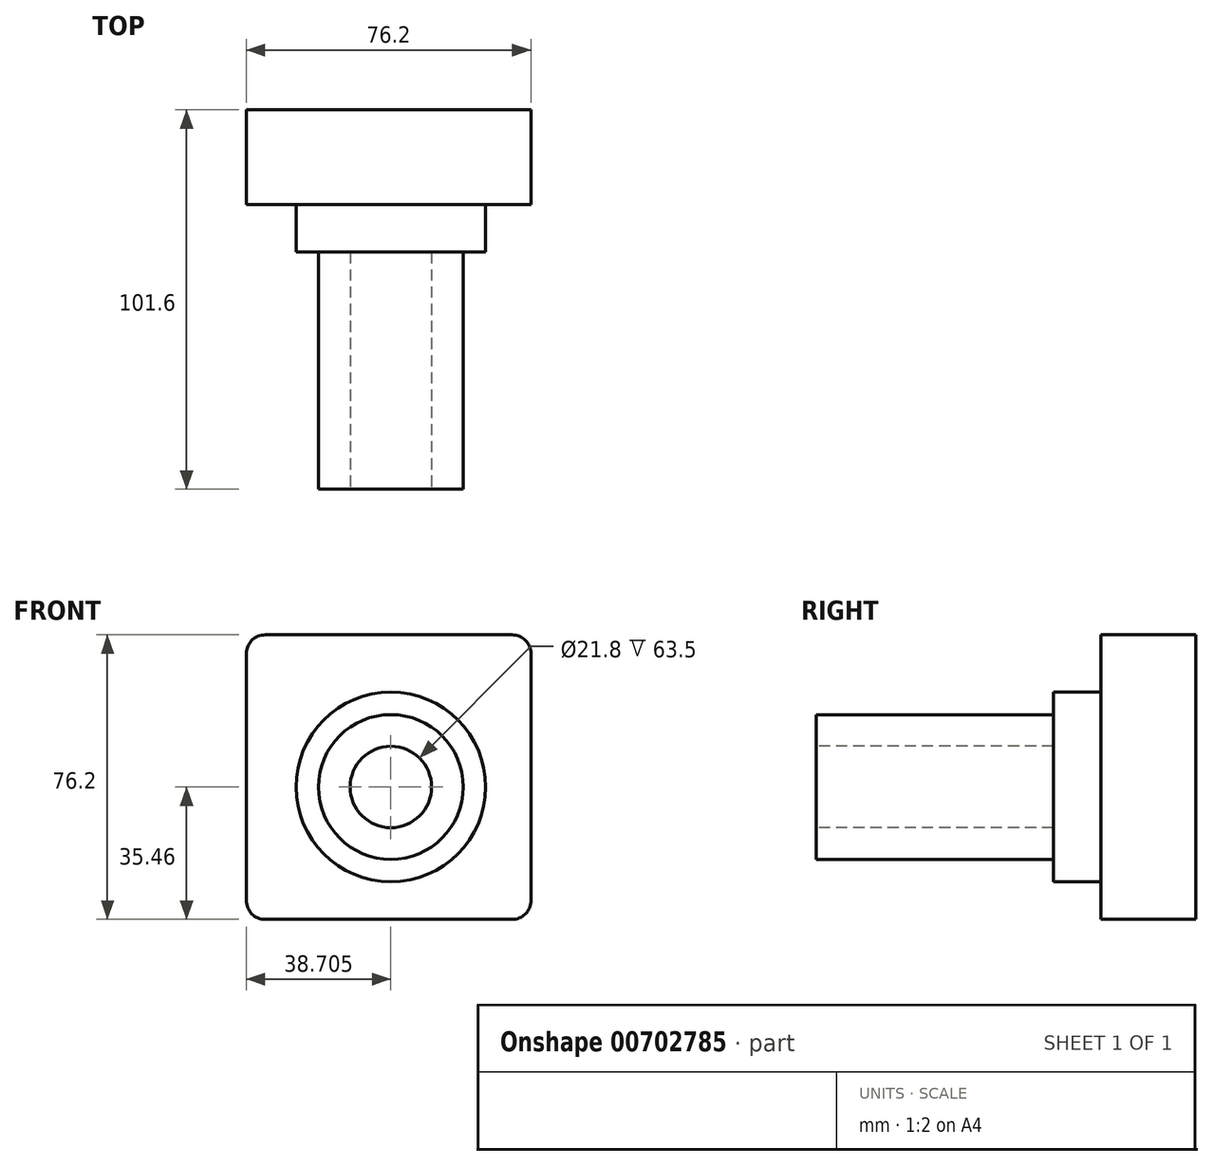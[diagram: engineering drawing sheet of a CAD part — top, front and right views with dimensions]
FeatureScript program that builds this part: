
annotation { "Feature Type Name" : "Feature", "Feature Type Description" : "" }
export const myFeature = defineFeature(function(context is Context, id is Id, definition is map)
    precondition{}
    {
        {
            var Q0;
            Q0=qCreatedBy(makeId("Front.planeOp"),FACE);
            var sketch = newSketch(context, id + "F0", { "sketchPlane" : qUnion([Q0])});
            skLineSegment(sketch, "E0.bottom", {"start": v(-33.86, 40.74) * mm, "end": v(42.34, 40.74) * mm});
            skLineSegment(sketch, "E0.top", {"start": v(-33.86, -35.46) * mm, "end": v(42.34, -35.46) * mm});
            skLineSegment(sketch, "E0.left", {"start": v(-33.86, 40.74) * mm, "end": v(-33.86, -35.46) * mm});
            skLineSegment(sketch, "E0.right", {"start": v(42.34, 40.74) * mm, "end": v(42.34, -35.46) * mm});
            skSolve(sketch);
        }
        {
            var Q0;
            Q0 = qSketchRegion(id + "F0", true);
            extrude(context, id + "F1", {"entities" : qUnion([Q0]), "depth" : 25.4 * mm, "offsetDistance" : 25.4 * mm});
        }
        {
            var Q0;
            Q0=makeQuery(id+"F1.opExtrude","SWEPT_EDGE",EDGE,{"disambiguationData":[OSD([sQuery(id+"F0.wireOp",EDGE,"E0.bottom"),sQuery(id+"F0.wireOp",EDGE,"E0.left")])]});
            var Q1;
            Q1=makeQuery(id+"F1.opExtrude","SWEPT_EDGE",EDGE,{"disambiguationData":[OSD([sQuery(id+"F0.wireOp",EDGE,"E0.bottom"),sQuery(id+"F0.wireOp",EDGE,"E0.right")])]});
            var Q2;
            Q2=makeQuery(id+"F1.opExtrude","SWEPT_EDGE",EDGE,{"disambiguationData":[OSD([sQuery(id+"F0.wireOp",EDGE,"E0.top"),sQuery(id+"F0.wireOp",EDGE,"E0.right")])]});
            var Q3;
            Q3=makeQuery(id+"F1.opExtrude","SWEPT_EDGE",EDGE,{"disambiguationData":[OSD([sQuery(id+"F0.wireOp",EDGE,"E0.top"),sQuery(id+"F0.wireOp",EDGE,"E0.left")])]});
            fillet(context, id + "F2", {"entities" : qUnion([Q0, Q1, Q2, Q3]), "radius" : 5.08 * mm, "tangentPropagation" : true, "allowEdgeOverflow" : false});
        }
        {
            var Q0;
            Q0=makeQuery(id+"F1.opExtrude","CAP_FACE",FACE,{"disambiguationData":[OSD([sQuery(id+"F0.wireOp",EDGE,"E0.bottom"),sQuery(id+"F0.wireOp",EDGE,"E0.top"),sQuery(id+"F0.wireOp",EDGE,"E0.left"),sQuery(id+"F0.wireOp",EDGE,"E0.right")])],"isStart":false});
            var sketch = newSketch(context, id + "F3", { "sketchPlane" : qUnion([Q0])});
            skCircle(sketch, "E1", {"center": v(4.84, 0) * mm, "radius": 25.38 * mm});
            skPoint(sketch, "E2.end.orphan", {"position": v(4.24, 40.74) * mm});
            skSolve(sketch);
        }
        {
            var Q0;
            Q0 = qSketchRegion(id + "F3", true);
            extrude(context, id + "F4", {"entities" : qUnion([Q0]), "operationType" : NewBodyOperationType.ADD, "depth" : 12.7 * mm, "offsetDistance" : 25.4 * mm});
        }
        {
            var Q0;
            Q0=makeQuery(id+"F4.opExtrude","CAP_FACE",FACE,{"disambiguationData":[OSD([sQuery(id+"F3.wireOp",EDGE,"E1")])],"isStart":false});
            var sketch = newSketch(context, id + "F5", { "sketchPlane" : qUnion([Q0])});
            skCircle(sketch, "E3", {"center": v(4.84, 0) * mm, "radius": 19.37 * mm});
            skSolve(sketch);
        }
        {
            var Q0;
            Q0 = qSketchRegion(id + "F5", true);
            extrude(context, id + "F6", {"entities" : qUnion([Q0]), "operationType" : NewBodyOperationType.ADD, "depth" : 63.5 * mm, "offsetDistance" : 25.4 * mm});
        }
        {
            var Q0;
            Q0=makeQuery(id+"F6.opExtrude","CAP_FACE",FACE,{"disambiguationData":[OSD([sQuery(id+"F5.wireOp",EDGE,"E3")])],"isStart":false});
            var sketch = newSketch(context, id + "F7", { "sketchPlane" : qUnion([Q0])});
            skCircle(sketch, "E4", {"center": v(4.84, 0) * mm, "radius": 10.9 * mm});
            skSolve(sketch);
        }
        {
            var Q0;
            Q0 = qSketchRegion(id + "F7", true);
            extrude(context, id + "F8", {"entities" : qUnion([Q0]), "operationType" : NewBodyOperationType.REMOVE, "oppositeDirection" : true, "depth" : 63.5 * mm, "offsetDistance" : 25.4 * mm});
        }
    });
